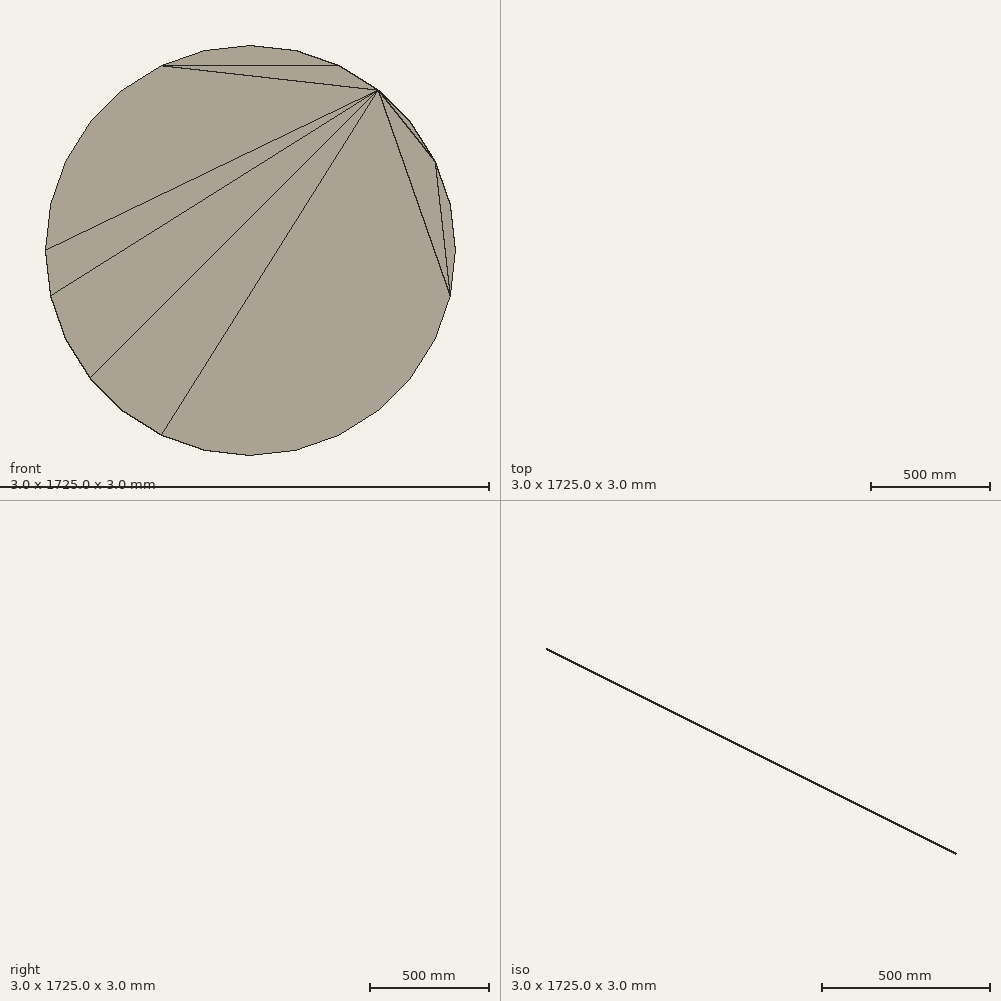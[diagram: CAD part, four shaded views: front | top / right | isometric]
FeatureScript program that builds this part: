
annotation { "Feature Type Name" : "Feature", "Feature Type Description" : "" }
export const myFeature = defineFeature(function(context is Context, id is Id, definition is map)
    precondition{}
    {
        {
            var Q0;
            Q0=qCreatedBy(makeId("Front.planeOp"),FACE);
            var sketch = newSketch(context, id + "F0", { "sketchPlane" : qUnion([Q0])});
            skCircle(sketch, "E0", {"center": v(0, 0) * mm, "radius": 1.5 * mm});
            skSolve(sketch);
        }
        {
            var Q0;
            Q0=makeQuery(id+"F0.imprint","IMPRINT",FACE,{"disambiguationData":[TD([[makeQuery(id+"F0.imprint","IMPRINT",EDGE,{"derivedFrom":sQuery(id+"F0.wireOp",EDGE,"E0")}),1.0]])]});
            extrude(context, id + "F1", {"entities" : qUnion([Q0]), "depth" : 1725 * mm, "offsetDistance" : 25 * mm});
        }
    });
